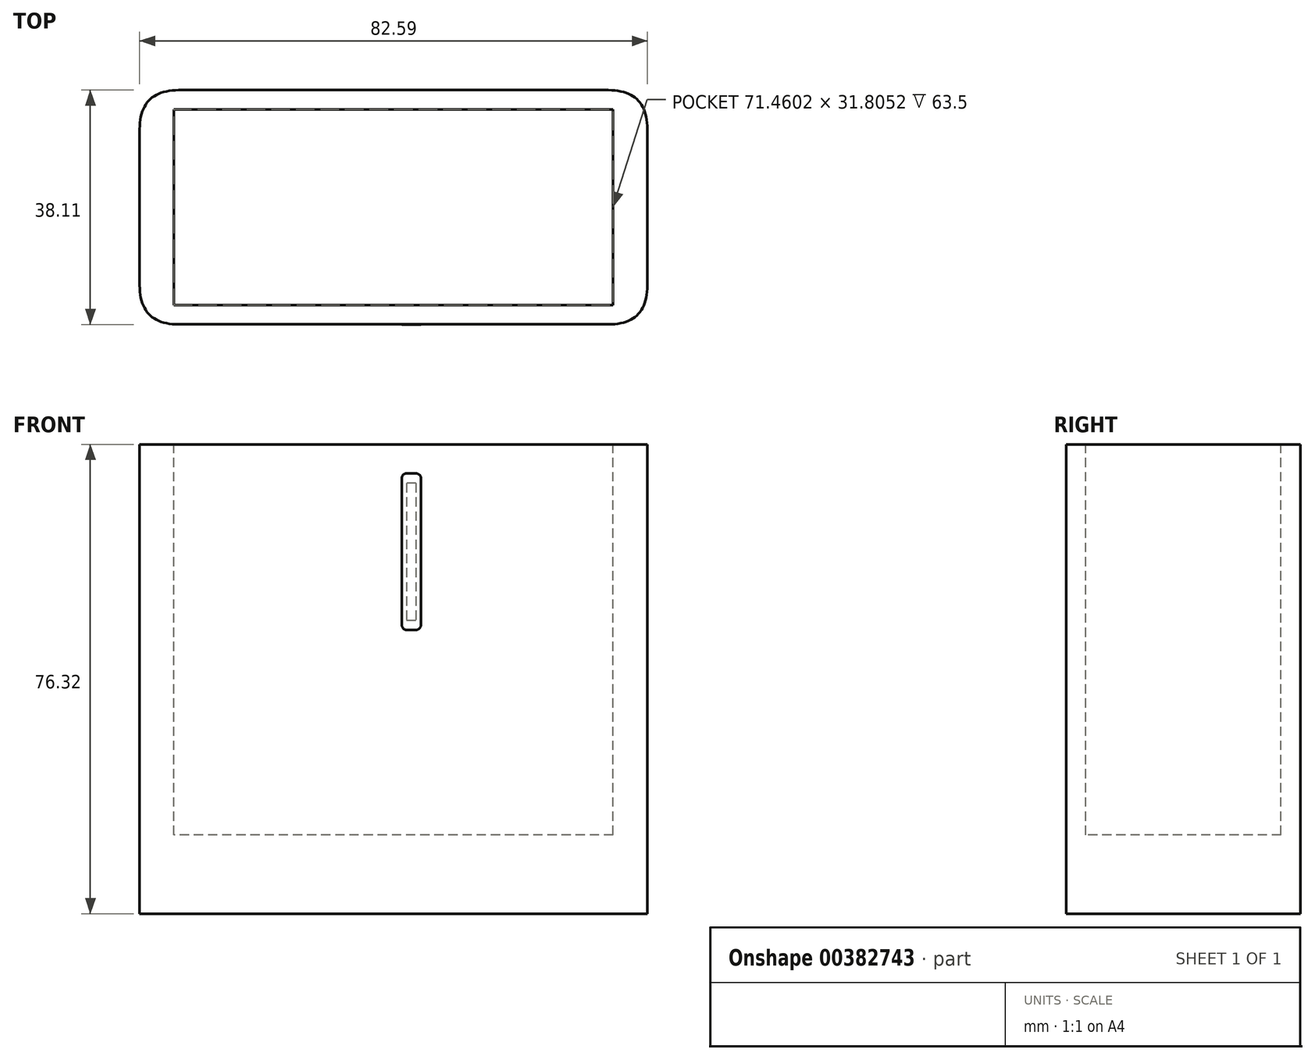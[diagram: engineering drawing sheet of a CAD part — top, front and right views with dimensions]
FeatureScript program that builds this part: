
annotation { "Feature Type Name" : "Feature", "Feature Type Description" : "" }
export const myFeature = defineFeature(function(context is Context, id is Id, definition is map)
    precondition{}
    {
        {
            var Q0;
            Q0=qCreatedBy(makeId("Front.planeOp"),FACE);
            var sketch = newSketch(context, id + "F0", { "sketchPlane" : qUnion([Q0])});
            skLineSegment(sketch, "E0", {"start": v(-32.63, 45.72) * mm, "end": v(-32.63, -30.6) * mm});
            skLineSegment(sketch, "E1", {"start": v(-32.63, -30.6) * mm, "end": v(49.96, -30.6) * mm});
            skLineSegment(sketch, "E2", {"start": v(49.96, -30.6) * mm, "end": v(49.96, 45.72) * mm});
            skLineSegment(sketch, "E3", {"start": v(49.96, 45.72) * mm, "end": v(-32.63, 45.72) * mm});
            skSolve(sketch);
        }
        {
            var Q0;
            Q0=makeQuery(id+"F0.imprint","IMPRINT",FACE,{"disambiguationData":[TD([[makeQuery(id+"F0.imprint","IMPRINT",EDGE,{"derivedFrom":sQuery(id+"F0.wireOp",EDGE,"E0")}),1.0]])]});
            extrude(context, id + "F1", {"entities" : qUnion([Q0]), "depth" : 25.4 * mm});
        }
        {
            var Q0;
            Q0=makeQuery(id+"F1.opExtrude","SWEPT_FACE",FACE,{"disambiguationData":[OSD([sQuery(id+"F0.wireOp",EDGE,"E3")])]});
            var sketch = newSketch(context, id + "F2", { "sketchPlane" : qUnion([Q0])});
            skSolve(sketch);
        }
        {
            var Q0;
            Q0=makeQuery(id+"F1.opExtrude","CAP_FACE",FACE,{"disambiguationData":[OSD([sQuery(id+"F0.wireOp",EDGE,"E0"),sQuery(id+"F0.wireOp",EDGE,"E1"),sQuery(id+"F0.wireOp",EDGE,"E2"),sQuery(id+"F0.wireOp",EDGE,"E3")])],"isStart":false});
            extrude(context, id + "F3", {"entities" : qUnion([Q0]), "operationType" : NewBodyOperationType.ADD, "depth" : 12.7 * mm});
        }
        {
            var Q0;
            {var subQ0=sQuery(id+"F0.wireOp",EDGE,"E3");Q0=makeQuery(id+"F3.boolean.opBoolean","MERGE",FACE,{"derivedFrom":[makeQuery(id+"F1.opExtrude","SWEPT_FACE",FACE,{"disambiguationData":[OSD([subQ0])]}),makeQuery(id+"F3.opExtrude","SWEPT_FACE",FACE,{"disambiguationData":[OSD([subQ0])]})]});}
            var sketch = newSketch(context, id + "F4", { "sketchPlane" : qUnion([Q0])});
            skLineSegment(sketch, "E4.bottom", {"start": v(44.4, -3.15) * mm, "end": v(-27.07, -3.15) * mm});
            skLineSegment(sketch, "E4.top", {"start": v(44.4, -34.95) * mm, "end": v(-27.07, -34.95) * mm});
            skLineSegment(sketch, "E4.left", {"start": v(44.4, -3.15) * mm, "end": v(44.4, -34.95) * mm});
            skLineSegment(sketch, "E4.right", {"start": v(-27.07, -3.15) * mm, "end": v(-27.07, -34.95) * mm});
            skPoint(sketch, "E4.middle", {"position": v(8.66, -19.05) * mm});
            skPoint(sketch, "E4.middle.positionSnap0", {"position": v(-32.63, -19.05) * mm});
            skPoint(sketch, "E4.middle.positionSnap1", {"position": v(8.66, 0) * mm});
            skPoint(sketch, "E4.centerSnap0", {"position": v(-32.63, -19.05) * mm});
            skPoint(sketch, "E4.centerSnap1", {"position": v(8.66, 0) * mm});
            skSolve(sketch);
        }
        {
            var Q0;
            Q0=makeQuery(id+"F4.imprint","IMPRINT",FACE,{"disambiguationData":[TD([[makeQuery(id+"F4.imprint","IMPRINT",EDGE,{"derivedFrom":sQuery(id+"F4.wireOp",EDGE,"E4.bottom")}),1.0]])]});
            extrude(context, id + "F5", {"entities" : qUnion([Q0]), "operationType" : NewBodyOperationType.REMOVE, "oppositeDirection" : true, "depth" : 63.5 * mm});
        }
        {
            var Q0;
            Q0=makeQuery(id+"F3.opExtrude","CAP_FACE",FACE,{"disambiguationData":[OSD([sQuery(id+"F0.wireOp",EDGE,"E0"),sQuery(id+"F0.wireOp",EDGE,"E1"),sQuery(id+"F0.wireOp",EDGE,"E2"),sQuery(id+"F0.wireOp",EDGE,"E3")])],"isStart":false});
            var sketch = newSketch(context, id + "F6", { "sketchPlane" : qUnion([Q0])});
            skLineSegment(sketch, "E5", {"start": v(49.96, 45.72) * mm, "end": v(12.33, 45.72) * mm});
            skLineSegment(sketch, "E6", {"start": v(49.96, 45.72) * mm, "end": v(49.96, 39.4) * mm});
            skLineSegment(sketch, "E7", {"start": v(12.33, 39.4) * mm, "end": v(10.8, 39.4) * mm});
            skLineSegment(sketch, "E8", {"start": v(10.8, 39.4) * mm, "end": v(10.8, 17.15) * mm});
            skLineSegment(sketch, "E9", {"start": v(10.8, 17.15) * mm, "end": v(12.33, 17.15) * mm});
            skLineSegment(sketch, "E10", {"start": v(12.33, 39.4) * mm, "end": v(12.33, 17.15) * mm});
            skSolve(sketch);
        }
        {
            var Q0;
            Q0=makeQuery(id+"F6.imprint","IMPRINT",FACE,{"disambiguationData":[TD([[makeQuery(id+"F6.imprint","IMPRINT",EDGE,{"derivedFrom":sQuery(id+"F6.wireOp",EDGE,"E7")}),1.0]])]});
            extrude(context, id + "F7", {"entities" : qUnion([Q0]), "operationType" : NewBodyOperationType.ADD, "depth" : 1 / 203.2 * mm});
        }
        {
            var Q0;
            Q0=makeQuery(id+"F7.opExtrude","CAP_FACE",FACE,{"disambiguationData":[OSD([sQuery(id+"F6.wireOp",EDGE,"E7"),sQuery(id+"F6.wireOp",EDGE,"E8"),sQuery(id+"F6.wireOp",EDGE,"E9"),sQuery(id+"F6.wireOp",EDGE,"E10")])],"isStart":false});
            var sketch = newSketch(context, id + "F8", { "sketchPlane" : qUnion([Q0])});
            skLineSegment(sketch, "E11", {"start": v(10.02, 39.4) * mm, "end": v(10.02, 41) * mm});
            skPoint(sketch, "E12.endSnap0", {"position": v(11.56, 39.4) * mm});
            skLineSegment(sketch, "E13.MirrorCS", {"start": v(13.1, 39.4) * mm, "end": v(13.1, 41) * mm});
            skPoint(sketch, "E14.endSnap0", {"position": v(12.33, 28.27) * mm});
            skLineSegment(sketch, "E15.MirrorCS", {"start": v(13.1, 17.15) * mm, "end": v(13.1, 15.55) * mm});
            skLineSegment(sketch, "E16.MirrorCS", {"start": v(10.02, 17.15) * mm, "end": v(10.02, 15.55) * mm});
            skLineSegment(sketch, "E17", {"start": v(10.02, 41) * mm, "end": v(13.1, 41) * mm});
            skLineSegment(sketch, "E18", {"start": v(10.02, 15.55) * mm, "end": v(13.1, 15.55) * mm});
            skLineSegment(sketch, "E19", {"start": v(13.1, 17.15) * mm, "end": v(13.1, 39.4) * mm});
            skLineSegment(sketch, "E20", {"start": v(10.02, 39.4) * mm, "end": v(10.02, 17.15) * mm});
            skSolve(sketch);
        }
        {
            var Q0;
            Q0 = qSketchRegion(id + "F8", true);
            extrude(context, id + "F9", {"entities" : qUnion([Q0]), "depth" : 1 / 406.4 * mm});
        }
        {
            var Q0;
            Q0=makeQuery(id+"F9.opExtrude","SWEPT_EDGE",EDGE,{"disambiguationData":[OSD([sQuery(id+"F8.wireOp",EDGE,"E13.MirrorCS"),sQuery(id+"F8.wireOp",EDGE,"E17")])]});
            var Q1;
            Q1=makeQuery(id+"F9.opExtrude","SWEPT_EDGE",EDGE,{"disambiguationData":[OSD([sQuery(id+"F8.wireOp",EDGE,"E11"),sQuery(id+"F8.wireOp",EDGE,"E17")])]});
            var Q2;
            Q2=makeQuery(id+"F9.opExtrude","SWEPT_EDGE",EDGE,{"disambiguationData":[OSD([sQuery(id+"F8.wireOp",EDGE,"E15.MirrorCS"),sQuery(id+"F8.wireOp",EDGE,"E18")])]});
            var Q3;
            Q3=makeQuery(id+"F9.opExtrude","SWEPT_EDGE",EDGE,{"disambiguationData":[OSD([sQuery(id+"F8.wireOp",EDGE,"E16.MirrorCS"),sQuery(id+"F8.wireOp",EDGE,"E18")])]});
            fillet(context, id + "F10", {"entities" : qUnion([Q0, Q1, Q2, Q3]), "radius" : 0.76 * mm, "tangentPropagation" : true, "allowEdgeOverflow" : false});
        }
        {
            var Q0;
            Q0=makeQuery(id+"F1.opExtrude","CAP_EDGE",EDGE,{"disambiguationData":[OSD([sQuery(id+"F0.wireOp",EDGE,"E0")])],"isStart":true});
            var Q1;
            Q1=makeQuery(id+"F3.opExtrude","CAP_EDGE",EDGE,{"disambiguationData":[OSD([sQuery(id+"F0.wireOp",EDGE,"E0")])],"isStart":false});
            var Q2;
            Q2=makeQuery(id+"F1.opExtrude","CAP_EDGE",EDGE,{"disambiguationData":[OSD([sQuery(id+"F0.wireOp",EDGE,"E2")])],"isStart":true});
            var Q3;
            Q3=makeQuery(id+"F3.opExtrude","CAP_EDGE",EDGE,{"disambiguationData":[OSD([sQuery(id+"F0.wireOp",EDGE,"E2")])],"isStart":false});
            fillet(context, id + "F11", {"entities" : qUnion([Q0, Q1, Q2, Q3]), "radius" : 6.35 * mm, "rho" : 0.5, "crossSection" : FilletCrossSection.CONIC, "allowEdgeOverflow" : false});
        }
    });
